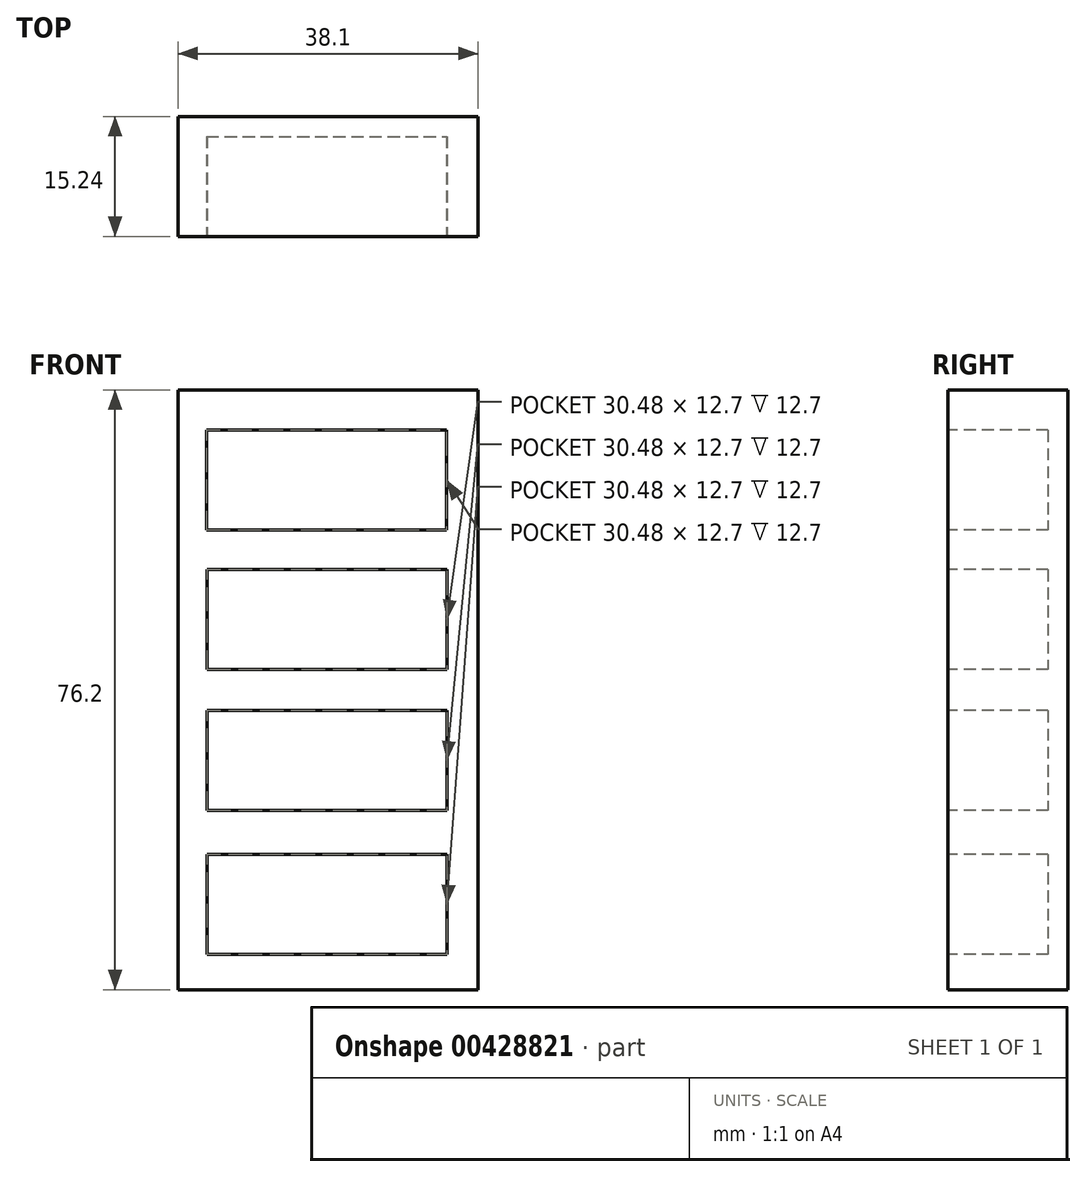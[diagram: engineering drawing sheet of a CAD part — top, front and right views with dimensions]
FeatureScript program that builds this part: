
annotation { "Feature Type Name" : "Feature", "Feature Type Description" : "" }
export const myFeature = defineFeature(function(context is Context, id is Id, definition is map)
    precondition{}
    {
        {
            var Q0;
            Q0=qCreatedBy(makeId("Front.planeOp"),FACE);
            var sketch = newSketch(context, id + "F0", { "sketchPlane" : qUnion([Q0])});
            skLineSegment(sketch, "E0.bottom", {"start": v(0, 0) * mm, "end": v(38.1, 0) * mm});
            skLineSegment(sketch, "E0.top", {"start": v(0, 76.2) * mm, "end": v(38.1, 76.2) * mm});
            skLineSegment(sketch, "E0.left", {"start": v(0, 0) * mm, "end": v(0, 76.2) * mm});
            skLineSegment(sketch, "E0.right", {"start": v(38.1, 0) * mm, "end": v(38.1, 76.2) * mm});
            skSolve(sketch);
        }
        {
            var Q0;
            Q0 = qSketchRegion(id + "F0", true);
            extrude(context, id + "F1", {"entities" : qUnion([Q0]), "depth" : 15.24 * mm});
        }
        {
            var Q0;
            Q0=makeQuery(id+"F1.opExtrude","CAP_FACE",FACE,{"disambiguationData":[OSD([sQuery(id+"F0.wireOp",EDGE,"E0.bottom"),sQuery(id+"F0.wireOp",EDGE,"E0.top"),sQuery(id+"F0.wireOp",EDGE,"E0.left"),sQuery(id+"F0.wireOp",EDGE,"E0.right")])],"isStart":false});
            var sketch = newSketch(context, id + "F2", { "sketchPlane" : qUnion([Q0])});
            skLineSegment(sketch, "E1.bottom", {"start": v(3.67, 53.38) * mm, "end": v(34.15, 53.38) * mm});
            skLineSegment(sketch, "E1.top", {"start": v(3.67, 40.68) * mm, "end": v(34.15, 40.68) * mm});
            skLineSegment(sketch, "E1.left", {"start": v(3.67, 53.38) * mm, "end": v(3.67, 40.68) * mm});
            skLineSegment(sketch, "E1.right", {"start": v(34.15, 53.38) * mm, "end": v(34.15, 40.68) * mm});
            skLineSegment(sketch, "E2.bottom", {"start": v(3.67, 35.45) * mm, "end": v(34.15, 35.45) * mm});
            skLineSegment(sketch, "E2.top", {"start": v(3.67, 22.75) * mm, "end": v(34.15, 22.75) * mm});
            skLineSegment(sketch, "E2.left", {"start": v(3.67, 35.45) * mm, "end": v(3.67, 22.75) * mm});
            skLineSegment(sketch, "E2.right", {"start": v(34.15, 35.45) * mm, "end": v(34.15, 22.75) * mm});
            skLineSegment(sketch, "E3.bottom", {"start": v(3.67, 17.2) * mm, "end": v(34.15, 17.2) * mm});
            skLineSegment(sketch, "E3.top", {"start": v(3.67, 4.5) * mm, "end": v(34.15, 4.5) * mm});
            skLineSegment(sketch, "E3.left", {"start": v(3.67, 17.2) * mm, "end": v(3.67, 4.5) * mm});
            skLineSegment(sketch, "E3.right", {"start": v(34.15, 17.2) * mm, "end": v(34.15, 4.5) * mm});
            skLineSegment(sketch, "E4.bottom", {"start": v(3.6, 71.07) * mm, "end": v(34.08, 71.07) * mm});
            skLineSegment(sketch, "E4.top", {"start": v(3.6, 58.37) * mm, "end": v(34.08, 58.37) * mm});
            skLineSegment(sketch, "E4.left", {"start": v(3.6, 71.07) * mm, "end": v(3.6, 58.37) * mm});
            skLineSegment(sketch, "E4.right", {"start": v(34.08, 71.07) * mm, "end": v(34.08, 58.37) * mm});
            skSolve(sketch);
        }
        {
            var Q0;
            Q0 = qSketchRegion(id + "F2", true);
            extrude(context, id + "F3", {"entities" : qUnion([Q0]), "operationType" : NewBodyOperationType.REMOVE, "oppositeDirection" : true, "depth" : 12.7 * mm});
        }
    });
